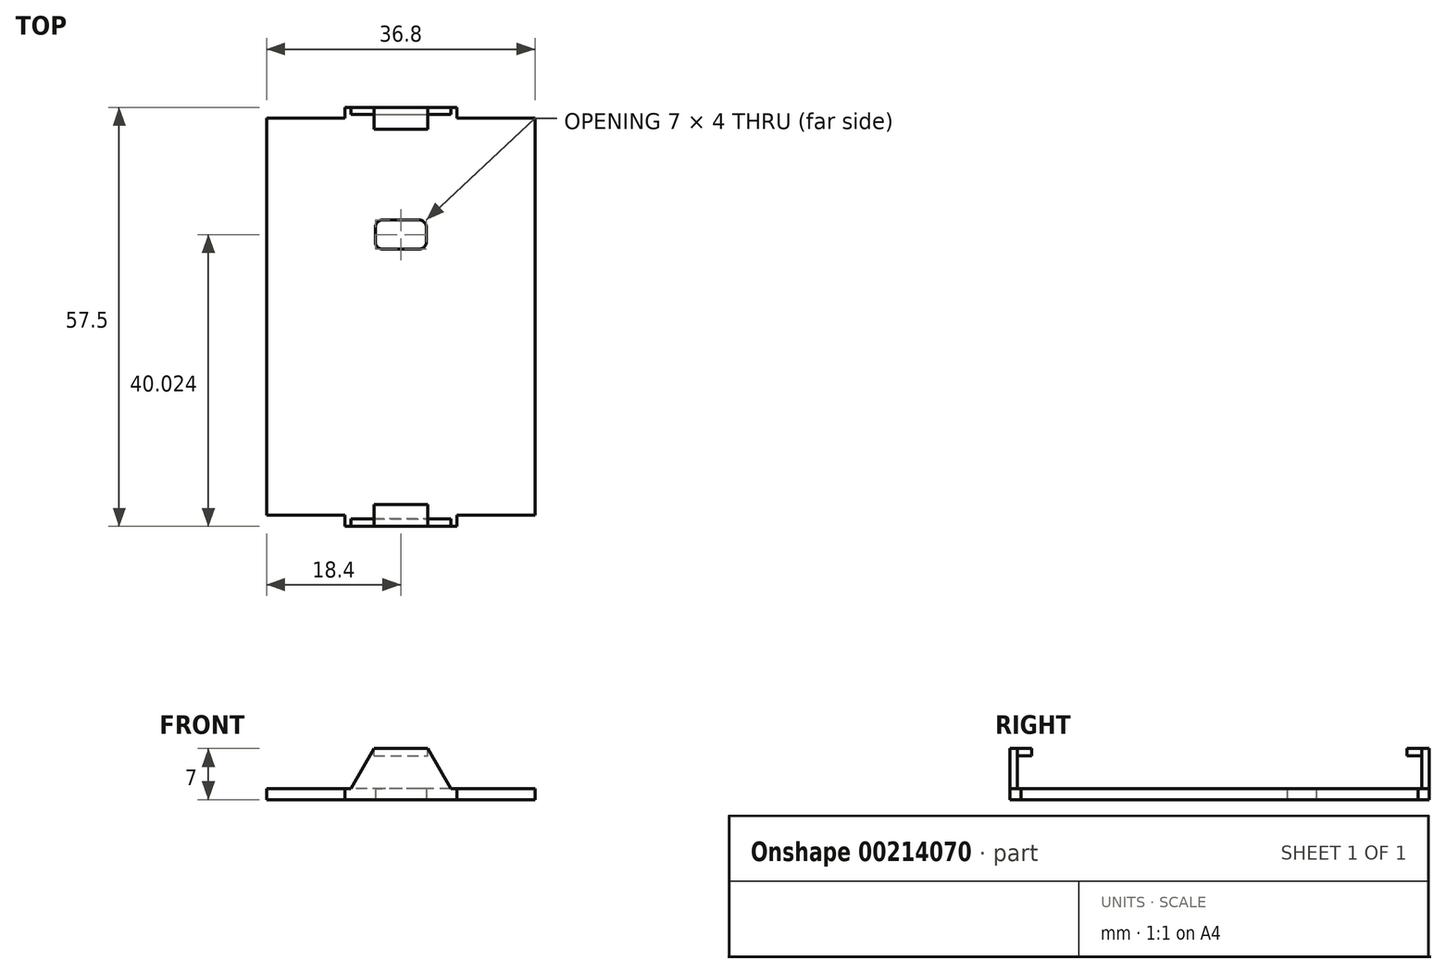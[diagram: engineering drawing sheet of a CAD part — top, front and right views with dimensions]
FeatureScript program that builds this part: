
annotation { "Feature Type Name" : "Feature", "Feature Type Description" : "" }
export const myFeature = defineFeature(function(context is Context, id is Id, definition is map)
    precondition{}
    {
        {
            var Q0;
            Q0=qCreatedBy(makeId("Top.planeOp"),FACE);
            var sketch = newSketch(context, id + "F0", { "sketchPlane" : qUnion([Q0])});
            skPoint(sketch, "E0.middle", {"position": v(0, 0) * mm});
            skLineSegment(sketch, "E1.bottom", {"start": v(18.4, -27.25) * mm, "end": v(-18.4, -27.25) * mm});
            skLineSegment(sketch, "E1.top", {"start": v(18.4, 27.25) * mm, "end": v(-18.4, 27.25) * mm});
            skLineSegment(sketch, "E1.left", {"start": v(18.4, -27.25) * mm, "end": v(18.4, 27.25) * mm});
            skLineSegment(sketch, "E1.right", {"start": v(-18.4, -27.25) * mm, "end": v(-18.4, 27.25) * mm});
            skLineSegment(sketch, "E2.bottom", {"start": v(-18.4, 27.25) * mm, "end": v(18.4, 27.25) * mm});
            skLineSegment(sketch, "E3.bottom", {"start": v(-18.4, -27.25) * mm, "end": v(18.4, -27.25) * mm});
            skLineSegment(sketch, "E4.bottom", {"start": v(7.7, -27.75) * mm, "end": v(-7.7, -27.75) * mm});
            skLineSegment(sketch, "E4.top", {"start": v(7.7, -27.25) * mm, "end": v(-7.7, -27.25) * mm});
            skLineSegment(sketch, "E4.left", {"start": v(7.7, -27.75) * mm, "end": v(7.7, -27.25) * mm});
            skLineSegment(sketch, "E4.right", {"start": v(-7.7, -27.75) * mm, "end": v(-7.7, -27.25) * mm});
            skLineSegment(sketch, "E5.bottom", {"start": v(-7.7, 27.25) * mm, "end": v(7.7, 27.25) * mm});
            skLineSegment(sketch, "E5.top", {"start": v(-7.7, 27.75) * mm, "end": v(7.7, 27.75) * mm});
            skLineSegment(sketch, "E5.left", {"start": v(-7.7, 27.25) * mm, "end": v(-7.7, 27.75) * mm});
            skLineSegment(sketch, "E5.right", {"start": v(7.7, 27.25) * mm, "end": v(7.7, 27.75) * mm});
            skLineSegment(sketch, "E6.bottom", {"start": v(3.5, 13.27) * mm, "end": v(-3.5, 13.27) * mm});
            skLineSegment(sketch, "E6.top", {"start": v(3.5, 9.27) * mm, "end": v(-3.5, 9.27) * mm});
            skLineSegment(sketch, "E6.left", {"start": v(3.5, 13.27) * mm, "end": v(3.5, 9.27) * mm});
            skLineSegment(sketch, "E6.right", {"start": v(-3.5, 13.27) * mm, "end": v(-3.5, 9.27) * mm});
            skPoint(sketch, "E6.middle", {"position": v(0, 11.27) * mm});
            skSolve(sketch);
        }
        {
            var Q0;
            Q0 = qSketchRegion(id + "F0", true);
            extrude(context, id + "F1", {"entities" : qUnion([Q0]), "depth" : 1.5 * mm});
        }
        {
            var Q0;
            Q0=makeQuery(id+"F1.opExtrude","SWEPT_FACE",FACE,{"disambiguationData":[OSD([sQuery(id+"F0.wireOp",EDGE,"E4.bottom")])]});
            var sketch = newSketch(context, id + "F2", { "sketchPlane" : qUnion([Q0])});
            skLineSegment(sketch, "E7.bottom", {"start": v(-3.7, 0) * mm, "end": v(3.7, 0) * mm});
            skLineSegment(sketch, "E7.top", {"start": v(-3.7, 7) * mm, "end": v(3.7, 7) * mm});
            skLineSegment(sketch, "E7.left", {"start": v(-3.7, 0) * mm, "end": v(-3.7, 7) * mm});
            skLineSegment(sketch, "E7.right", {"start": v(3.7, 0) * mm, "end": v(3.7, 7) * mm});
            skLineSegment(sketch, "E8", {"start": v(-3.7, 6) * mm, "end": v(3.7, 6) * mm});
            skLineSegment(sketch, "E9", {"start": v(-3.7, 7) * mm, "end": v(-7.7, 0) * mm});
            skLineSegment(sketch, "E10", {"start": v(-7.7, 0) * mm, "end": v(7.7, 0) * mm});
            skLineSegment(sketch, "E11", {"start": v(7.7, 0) * mm, "end": v(3.7, 7) * mm});
            skSolve(sketch);
        }
        {
            var Q0;
            {var subQ0=sQuery(id+"F2.wireOp",EDGE,"E10");var subQ1=sQuery(id+"F2.wireOp",EDGE,"E7.left");var subQ2=makeQuery(id+"F2.imprint","INTERSECT",VERTEX,{"derivedFrom":[subQ1,subQ0]});Q0=makeQuery(id+"F2.imprint","IMPRINT",FACE,{"disambiguationData":[TD([[makeQuery(id+"F2.imprint","IMPRINT",EDGE,{"disambiguationData":[TD([[subQ2,-1.0]])],"derivedFrom":subQ1}),1.0]])]});}
            var Q1;
            {var subQ0=sQuery(id+"F2.wireOp",EDGE,"E10");var subQ1=sQuery(id+"F2.wireOp",EDGE,"E7.left");var subQ2=makeQuery(id+"F2.imprint","INTERSECT",VERTEX,{"derivedFrom":[subQ1,subQ0]});Q1=makeQuery(id+"F2.imprint","IMPRINT",FACE,{"disambiguationData":[TD([[makeQuery(id+"F2.imprint","IMPRINT",EDGE,{"disambiguationData":[TD([[subQ2,-1.0]])],"derivedFrom":subQ1}),-1.0]])]});}
            var Q2;
            {var subQ0=sQuery(id+"F2.wireOp",EDGE,"E10");var subQ1=sQuery(id+"F2.wireOp",EDGE,"E7.right");var subQ2=makeQuery(id+"F2.imprint","INTERSECT",VERTEX,{"derivedFrom":[subQ1,subQ0]});Q2=makeQuery(id+"F2.imprint","IMPRINT",FACE,{"disambiguationData":[TD([[makeQuery(id+"F2.imprint","IMPRINT",EDGE,{"disambiguationData":[TD([[subQ2,-1.0]])],"derivedFrom":subQ1}),-1.0]])]});}
            var Q3;
            {var subQ0=sQuery(id+"F2.wireOp",EDGE,"E7.left");var subQ1=makeQuery(id+"F2.imprint","INTERSECT",VERTEX,{"derivedFrom":[subQ0,sQuery(id+"F2.wireOp",EDGE,"E8")]});Q3=makeQuery(id+"F2.imprint","IMPRINT",FACE,{"disambiguationData":[TD([[makeQuery(id+"F2.imprint","IMPRINT",EDGE,{"disambiguationData":[TD([[subQ1,1.0]])],"derivedFrom":subQ0}),1.0]])]});}
            var Q4;
            {var subQ0=sQuery(id+"F2.wireOp",EDGE,"E8");Q4=makeQuery(id+"F2.imprint","IMPRINT",FACE,{"disambiguationData":[TD([[makeQuery(id+"F2.imprint","IMPRINT",EDGE,{"derivedFrom":subQ0}),-1.0]])]});}
            var Q5;
            {var subQ0=sQuery(id+"F2.wireOp",EDGE,"E7.top");Q5=makeQuery(id+"F2.imprint","IMPRINT",FACE,{"disambiguationData":[TD([[makeQuery(id+"F2.imprint","IMPRINT",EDGE,{"derivedFrom":subQ0}),-1.0]])]});}
            var Q6;
            {var subQ0=sQuery(id+"F2.wireOp",EDGE,"E7.right");var subQ1=makeQuery(id+"F2.imprint","INTERSECT",VERTEX,{"derivedFrom":[subQ0,sQuery(id+"F2.wireOp",EDGE,"E8")]});Q6=makeQuery(id+"F2.imprint","IMPRINT",FACE,{"disambiguationData":[TD([[makeQuery(id+"F2.imprint","IMPRINT",EDGE,{"disambiguationData":[TD([[subQ1,1.0]])],"derivedFrom":subQ0}),-1.0]])]});}
            var Q7;
            {var subQ1=sQuery(id+"F0.wireOp",EDGE,"E4.bottom");var subQ2=makeQuery(id+"F1.opExtrude","SWEPT_EDGE",EDGE,{"disambiguationData":[OSD([subQ1,sQuery(id+"F0.wireOp",EDGE,"E4.left")])]});Q7=makeQuery(id+"F2.imprint","IMPRINT",FACE,{"disambiguationData":[TD([[makeQuery(id+"F2.imprint","IMPRINT",EDGE,{"derivedFrom":subQ2}),-1.0]])]});}
            var Q8;
            {var subQ1=sQuery(id+"F0.wireOp",EDGE,"E4.bottom");var subQ2=makeQuery(id+"F1.opExtrude","SWEPT_EDGE",EDGE,{"disambiguationData":[OSD([subQ1,sQuery(id+"F0.wireOp",EDGE,"E4.right")])]});Q8=makeQuery(id+"F2.imprint","IMPRINT",FACE,{"disambiguationData":[TD([[makeQuery(id+"F2.imprint","IMPRINT",EDGE,{"derivedFrom":subQ2}),1.0]])]});}
            extrude(context, id + "F3", {"entities" : qUnion([Q0, Q1, Q2, Q3, Q4, Q5, Q6, Q7, Q8]), "depth" : 1 * mm});
        }
        {
            var Q0;
            {var subQ0=sQuery(id+"F2.wireOp",EDGE,"E7.top");Q0=makeQuery(id+"F2.imprint","IMPRINT",FACE,{"disambiguationData":[TD([[makeQuery(id+"F2.imprint","IMPRINT",EDGE,{"derivedFrom":subQ0}),-1.0]])]});}
            extrude(context, id + "F4", {"entities" : qUnion([Q0]), "oppositeDirection" : true, "depth" : 2 * mm});
        }
        {
            var Q0;
            Q0=makeQuery(id+"F3.opExtrude","SWEPT_BODY",BODY,{"disambiguationData":[OSD([sQuery(id+"F0.wireOp",EDGE,"E4.bottom"),sQuery(id+"F0.wireOp",EDGE,"E4.left"),sQuery(id+"F0.wireOp",EDGE,"E4.right"),sQuery(id+"F2.wireOp",EDGE,"E7.top"),sQuery(id+"F2.wireOp",EDGE,"E9"),sQuery(id+"F2.wireOp",EDGE,"E10"),sQuery(id+"F2.wireOp",EDGE,"E11")])]});
            var Q1;
            Q1=makeQuery(id+"F4.opExtrude","SWEPT_BODY",BODY,{"disambiguationData":[OSD([sQuery(id+"F2.wireOp",EDGE,"E7.top"),sQuery(id+"F2.wireOp",EDGE,"E7.left"),sQuery(id+"F2.wireOp",EDGE,"E7.right"),sQuery(id+"F2.wireOp",EDGE,"E8")])]});
            var Q2;
            Q2=qCreatedBy(makeId("Front.planeOp"),FACE);
            mirror(context, id + "F5", {"operationType" : NewBodyOperationType.ADD, "entities" : qUnion([Q0, Q1]), "mirrorPlane" : qUnion([Q2])});
        }
        {
            var Q0;
            Q0=makeQuery(id+"F1.opExtrude","SWEPT_EDGE",EDGE,{"disambiguationData":[OSD([sQuery(id+"F0.wireOp",EDGE,"E6.bottom"),sQuery(id+"F0.wireOp",EDGE,"E6.right")])]});
            var Q1;
            Q1=makeQuery(id+"F1.opExtrude","SWEPT_EDGE",EDGE,{"disambiguationData":[OSD([sQuery(id+"F0.wireOp",EDGE,"E6.top"),sQuery(id+"F0.wireOp",EDGE,"E6.right")])]});
            var Q2;
            Q2=makeQuery(id+"F1.opExtrude","SWEPT_EDGE",EDGE,{"disambiguationData":[OSD([sQuery(id+"F0.wireOp",EDGE,"E6.top"),sQuery(id+"F0.wireOp",EDGE,"E6.left")])]});
            var Q3;
            Q3=makeQuery(id+"F1.opExtrude","SWEPT_EDGE",EDGE,{"disambiguationData":[OSD([sQuery(id+"F0.wireOp",EDGE,"E6.bottom"),sQuery(id+"F0.wireOp",EDGE,"E6.left")])]});
            fillet(context, id + "F6", {"entities" : qUnion([Q0, Q1, Q2, Q3]), "radius" : 1 * mm, "tangentPropagation" : true, "allowEdgeOverflow" : false});
        }
    });
